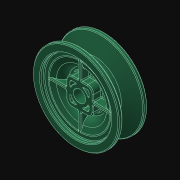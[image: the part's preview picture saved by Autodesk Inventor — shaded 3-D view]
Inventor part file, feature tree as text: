
AUTODESK INVENTOR PART (.ipt)
format: ipt  version: 2021.3 (Build 253353010, 353A)  size: 1,338,368 bytes
history: native  units: in
note: dims shown in document units (in); Inventor stores cm internally (conversion verified against a paired STEP export)
features: fillet x1, imported_body x1
ambient origin geometry x8: Origin, YZ Plane, XZ Plane, XY Plane, X Axis, Y Axis, Z Axis, Center Point
bodies: Body1 (feature_tree)
feature tree (2):
  fillet  "Fillet6"  [1 undecoded]
  imported_body  "Base1"
note: 1 required parameter value undecoded (feature->parameter linkage not recoverable at this tier; creation-order binding heuristic only, values carry confidence <= 0.55)
